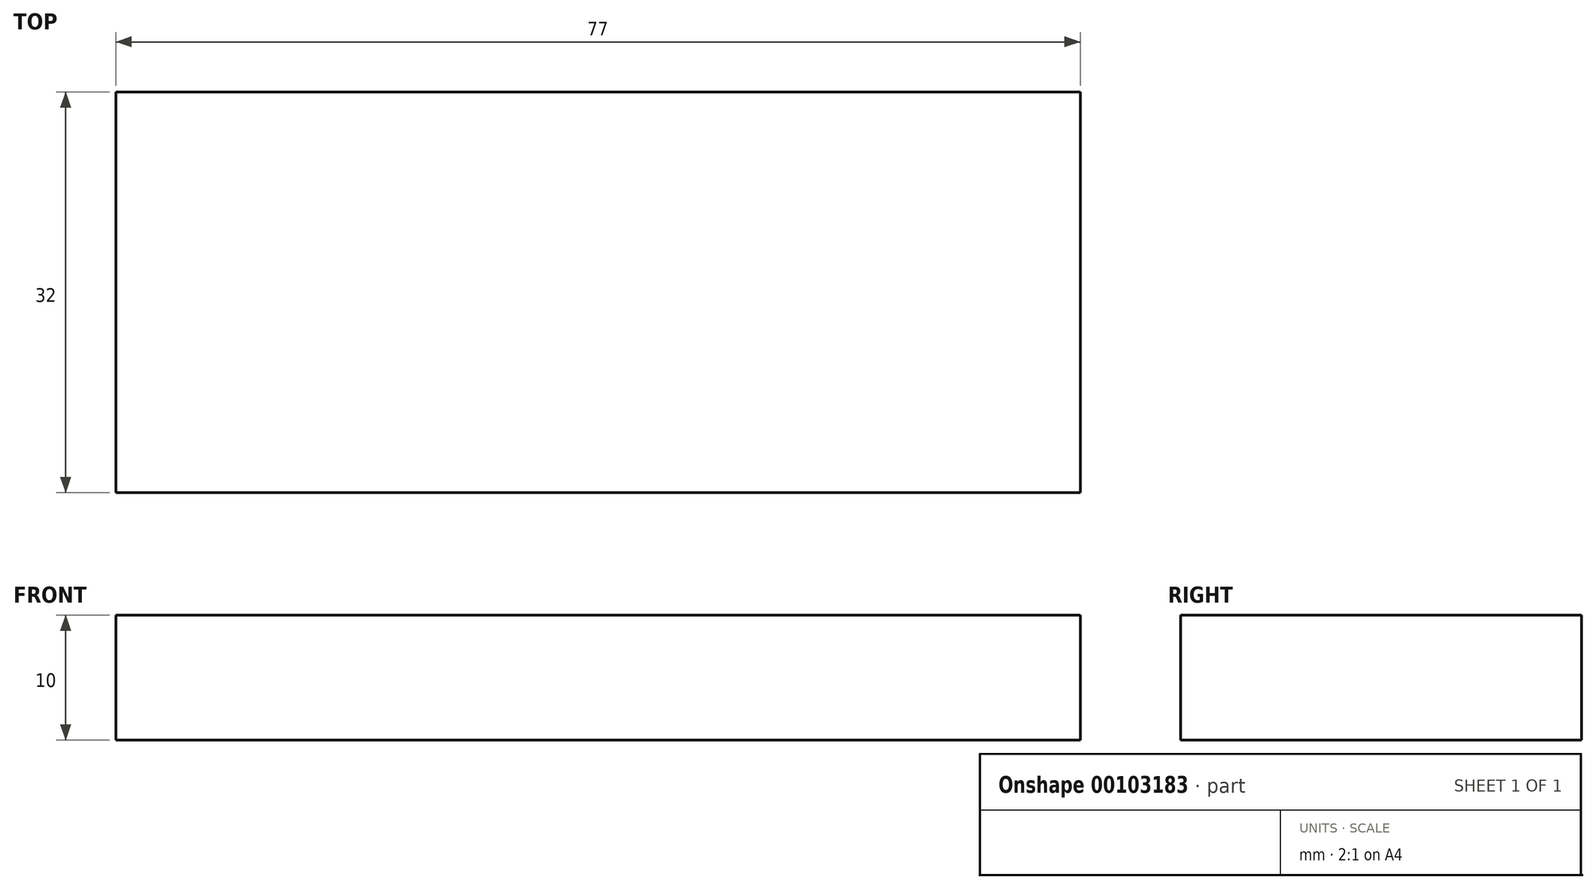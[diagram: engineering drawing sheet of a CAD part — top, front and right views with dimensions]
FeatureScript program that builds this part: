
annotation { "Feature Type Name" : "Feature", "Feature Type Description" : "" }
export const myFeature = defineFeature(function(context is Context, id is Id, definition is map)
    precondition{}
    {
        {
            var Q0;
            Q0=qCreatedBy(makeId("Top.planeOp"),FACE);
            var sketch = newSketch(context, id + "F0", { "sketchPlane" : qUnion([Q0])});
            skLineSegment(sketch, "E0.bottom", {"start": v(38.5, -16) * mm, "end": v(-38.5, -16) * mm});
            skLineSegment(sketch, "E0.top", {"start": v(38.5, 16) * mm, "end": v(-38.5, 16) * mm});
            skLineSegment(sketch, "E0.left", {"start": v(38.5, -16) * mm, "end": v(38.5, 16) * mm});
            skLineSegment(sketch, "E0.right", {"start": v(-38.5, -16) * mm, "end": v(-38.5, 16) * mm});
            skPoint(sketch, "E0.middle", {"position": v(0, 0) * mm});
            skSolve(sketch);
        }
        {
            var Q0;
            Q0=makeQuery(id+"F0.imprint","IMPRINT",FACE,{"disambiguationData":[TD([[makeQuery(id+"F0.imprint","IMPRINT",EDGE,{"derivedFrom":sQuery(id+"F0.wireOp",EDGE,"E0.bottom")}),-1.0]])]});
            extrude(context, id + "F1", {"entities" : qUnion([Q0]), "depth" : 10 * mm});
        }
    });
